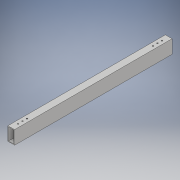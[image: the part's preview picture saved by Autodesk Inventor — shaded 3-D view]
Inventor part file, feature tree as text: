
AUTODESK INVENTOR PART (.ipt)
format: ipt  version: 2019 (Build 230136000, 136)  size: 137,728 bytes
history: native  units: mm
features: sketch x3, extrude x2, other x1, hole x1
ambient origin geometry x8: Origin, YZ Plane, XZ Plane, XY Plane, X Axis, Y Axis, Z Axis, Center Point
bodies: Body1 (feature_tree)
feature tree (7):
  other  "ソリッド1"
  extrude  "押し出し1"  Depth=15.0mm
  hole  "穴1"  [1 undecoded]
  extrude  "押し出し2"  Depth=350.0mm TaperAngle=0.0deg
  sketch  "スケッチ1"
  sketch  "スケッチ2"
  sketch  "スケッチ3"
note: 1 required parameter value undecoded (feature->parameter linkage not recoverable at this tier; creation-order binding heuristic only, values carry confidence <= 0.55)
